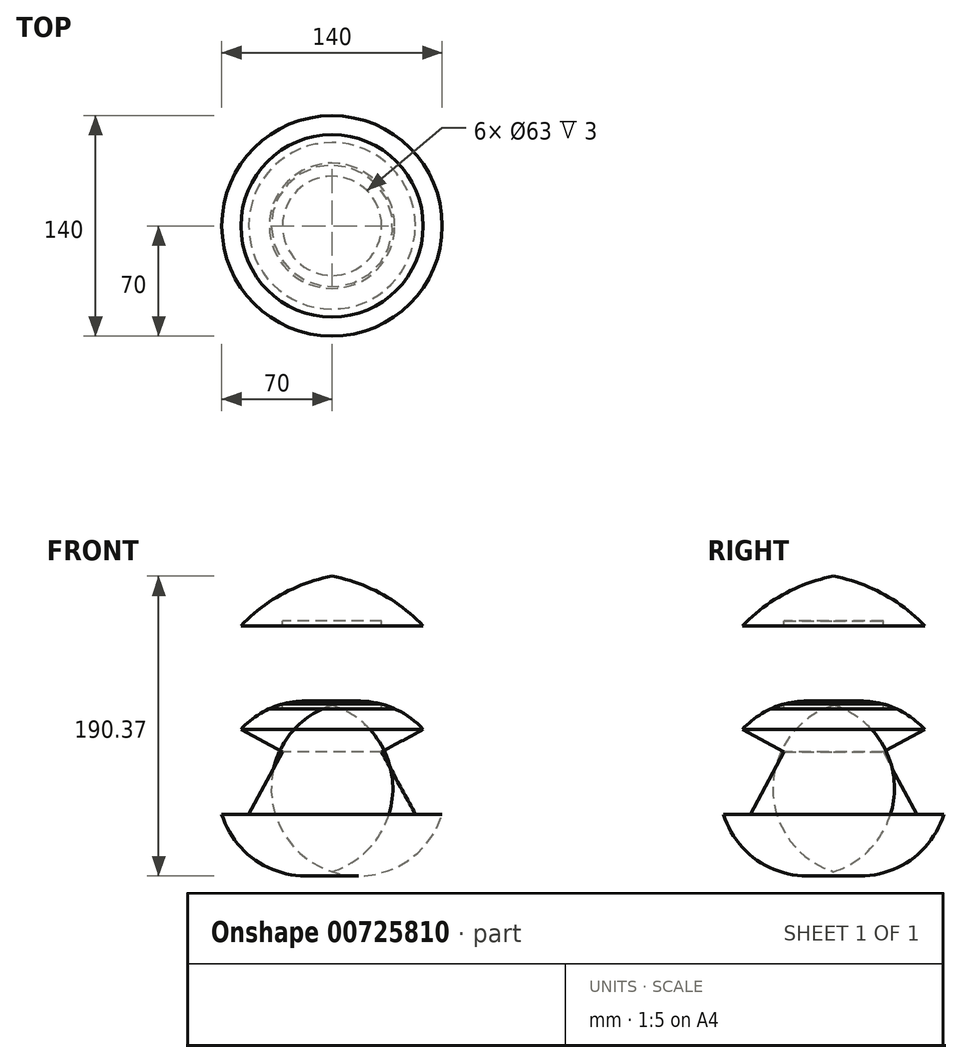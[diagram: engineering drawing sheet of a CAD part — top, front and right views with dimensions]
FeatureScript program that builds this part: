
annotation { "Feature Type Name" : "Feature", "Feature Type Description" : "" }
export const myFeature = defineFeature(function(context is Context, id is Id, definition is map)
    precondition{}
    {
        {
            var Q0;
            Q0=qCreatedBy(makeId("Front.planeOp"),FACE);
            var sketch = newSketch(context, id + "F0", { "sketchPlane" : qUnion([Q0])});
            skLineSegment(sketch, "E0", {"start": v(0, 74.85) * mm, "end": v(0, -76.41) * mm, "construction": true});
            skLineSegment(sketch, "E1", {"start": v(0, -6.41) * mm, "end": v(-31.5, -6.41) * mm, "construction": true});
            skArc(sketch, "E2", {"start": v(-31.5, -6.41) * mm, "mid": v(-65.57, -33.2) * mm, "end": v(-70, -76.32) * mm});
            skLineSegment(sketch, "E3", {"start": v(-31.5, -6.41) * mm, "end": v(-31.5, 43.35) * mm, "construction": true});
            skLineSegment(sketch, "E4", {"start": v(-31.5, -36.77) * mm, "end": v(-52.89, -76.36) * mm});
            skLineSegment(sketch, "E5", {"start": v(-31.5, -36.77) * mm, "end": v(-57.9, -22.51) * mm});
            skLineSegment(sketch, "E6", {"start": v(-31.5, -6.41) * mm, "end": v(-31.5, -9.41) * mm});
            skLineSegment(sketch, "E7", {"start": v(-31.5, -9.41) * mm, "end": v(-39.84, -9.41) * mm});
            skLineSegment(sketch, "E8", {"start": v(-31.5, -9.41) * mm, "end": v(-28.5, -9.41) * mm});
            skLineSegment(sketch, "E9", {"start": v(-70, -76.32) * mm, "end": v(-52.89, -76.36) * mm});
            skLineSegment(sketch, "E10", {"start": v(0, 74.85) * mm, "end": v(0, 43.35) * mm});
            skLineSegment(sketch, "E11", {"start": v(-57.9, -22.51) * mm, "end": v(-57.9, 43.35) * mm, "construction": true});
            skArc(sketch, "E12", {"start": v(0, 74.85) * mm, "mid": v(-31.4, 63.6) * mm, "end": v(-57.9, 43.35) * mm});
            skLineSegment(sketch, "E13", {"start": v(-31.5, 43.35) * mm, "end": v(-31.5, 46.35) * mm});
            skLineSegment(sketch, "E14", {"start": v(-31.5, 46.35) * mm, "end": v(0, 46.35) * mm});
            skLineSegment(sketch, "E15", {"start": v(-31.5, 43.35) * mm, "end": v(-57.9, 43.35) * mm});
            skLineSegment(sketch, "E16", {"start": v(0, -6.41) * mm, "end": v(34.31, -6.41) * mm, "construction": true});
            skLineSegment(sketch, "E17", {"start": v(34.31, -6.41) * mm, "end": v(34.31, -76.41) * mm, "construction": true});
            skLineSegment(sketch, "E18", {"start": v(34.31, -76.41) * mm, "end": v(-70, -76.32) * mm, "construction": true});
            skLineSegment(sketch, "E19", {"start": v(0, 46.35) * mm, "end": v(6.24, 46.35) * mm, "construction": true});
            skLineSegment(sketch, "E20", {"start": v(0, 74.85) * mm, "end": v(7.78, 76.35) * mm, "construction": true});
            skSolve(sketch);
        }
        {
            var Q0;
            {var subQ4=sQuery(id+"F0.wireOp",EDGE,"E4");Q0=makeQuery(id+"F0.imprint","IMPRINT",FACE,{"disambiguationData":[TD([[makeQuery(id+"F0.imprint","IMPRINT",EDGE,{"derivedFrom":subQ4}),-1.0]])]});}
            var Q1;
            Q1=sQuery(id+"F0.wireOp",EDGE,"sLKuqdue-0dgx-A74x-lwYk-sO1N8aTW291a");
            var Q2;
            Q2=sQuery(id+"F0.wireOp",EDGE,"E2");
            var Q3;
            Q3=sQuery(id+"F0.wireOp",EDGE,"jUqj5v6M-giF3-z9Rl-6BCL-GtmUUGOwKQBJ");
            var Q4;
            Q4=sQuery(id+"F0.wireOp",EDGE,"E0");
            revolve(context, id + "F1", {"surfaceOperationType" : NewSurfaceOperationType.NEW, "entities" : qUnion([Q0]), "surfaceEntities" : qUnion([Q1, Q2, Q3]), "axis" : qUnion([Q4]), "revolveType" : RevolveType.FULL});
        }
        {
            var Q0;
            Q0 = qSketchRegion(id + "F0", true);
            var Q1;
            Q1=sQuery(id+"F0.wireOp",EDGE,"E2");
            var Q2;
            Q2=sQuery(id+"F0.wireOp",EDGE,"jUqj5v6M-giF3-z9Rl-6BCL-GtmUUGOwKQBJ");
            var Q3;
            Q3=sQuery(id+"F0.wireOp",EDGE,"E8");
            var Q4;
            Q4=sQuery(id+"F0.wireOp",EDGE,"E0");
            revolve(context, id + "F2", {"bodyType" : ToolBodyType.SURFACE, "surfaceOperationType" : NewSurfaceOperationType.NEW, "entities" : qUnion([Q0]), "surfaceEntities" : qUnion([Q1, Q2, Q3]), "axis" : qUnion([Q4]), "revolveType" : RevolveType.FULL});
        }
        {
            var Q0;
            Q0 = qSketchRegion(id + "F0", true);
            var Q1;
            Q1=sQuery(id+"F0.wireOp",EDGE,"sLKuqdue-0dgx-A74x-lwYk-sO1N8aTW291a");
            var Q2;
            Q2=sQuery(id+"F0.wireOp",EDGE,"E0");
            revolve(context, id + "F3", {"surfaceOperationType" : NewSurfaceOperationType.NEW, "entities" : qUnion([Q0]), "surfaceEntities" : qUnion([Q1]), "axis" : qUnion([Q2]), "revolveType" : RevolveType.FULL});
        }
        {
            var Q0;
            {var subQ0=sQuery(id+"F0.wireOp",EDGE,"E6");Q0=makeQuery(id+"F0.imprint","IMPRINT",FACE,{"disambiguationData":[TD([[makeQuery(id+"F0.imprint","IMPRINT",EDGE,{"derivedFrom":subQ0}),-1.0]])]});}
            var Q1;
            Q1=sQuery(id+"F0.wireOp",EDGE,"E0");
            revolve(context, id + "F4", {"surfaceOperationType" : NewSurfaceOperationType.NEW, "entities" : qUnion([Q0]), "axis" : qUnion([Q1]), "revolveType" : RevolveType.FULL});
        }
    });
